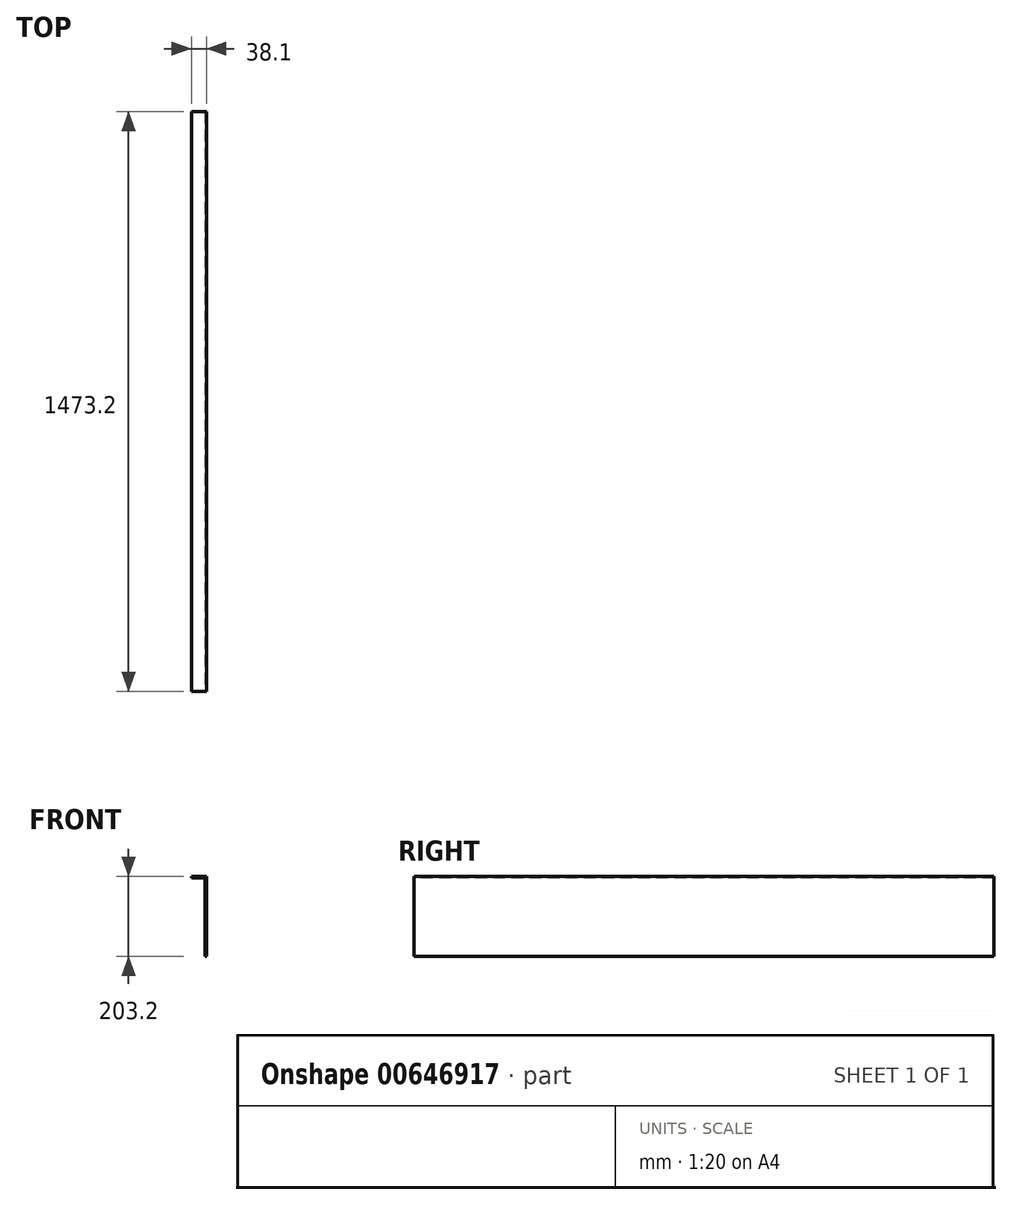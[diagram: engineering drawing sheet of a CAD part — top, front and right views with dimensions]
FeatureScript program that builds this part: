
annotation { "Feature Type Name" : "Feature", "Feature Type Description" : "" }
export const myFeature = defineFeature(function(context is Context, id is Id, definition is map)
    precondition{}
    {
        {
            var Q0;
            Q0=qCreatedBy(makeId("Front.planeOp"),FACE);
            var sketch = newSketch(context, id + "F0", { "sketchPlane" : qUnion([Q0])});
            skLineSegment(sketch, "E0", {"start": v(-36.51, 63.7) * mm, "end": v(-36.51, 60.52) * mm});
            skLineSegment(sketch, "E1", {"start": v(-36.51, 60.52) * mm, "end": v(-1.59, 60.52) * mm});
            skLineSegment(sketch, "E2", {"start": v(-1.59, 60.52) * mm, "end": v(-1.59, -139.5) * mm});
            skLineSegment(sketch, "E3", {"start": v(-1.59, -139.5) * mm, "end": v(1.59, -139.5) * mm});
            skLineSegment(sketch, "E4", {"start": v(1.59, -139.5) * mm, "end": v(1.59, 63.7) * mm});
            skLineSegment(sketch, "E5", {"start": v(1.59, 63.7) * mm, "end": v(-36.51, 63.7) * mm});
            skSolve(sketch);
        }
        {
            var Q0;
            Q0 = qSketchRegion(id + "F0", true);
            extrude(context, id + "F1", {"entities" : qUnion([Q0]), "oppositeDirection" : true, "depth" : 1473.2 * mm, "offsetDistance" : 25.4 * mm});
        }
    });
